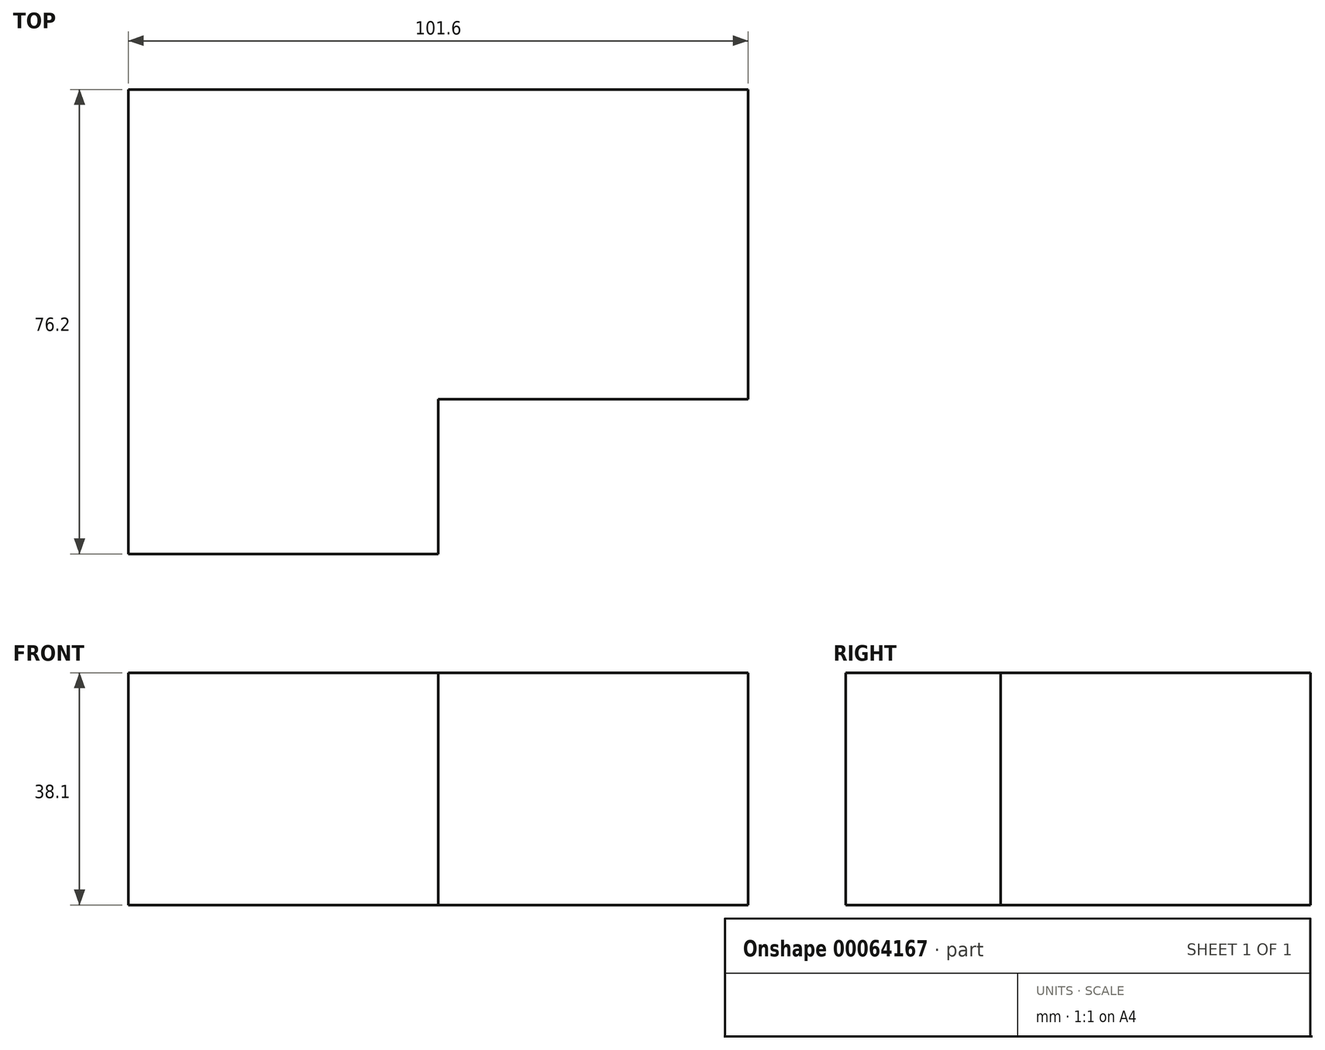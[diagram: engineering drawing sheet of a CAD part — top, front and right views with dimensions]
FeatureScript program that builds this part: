
annotation { "Feature Type Name" : "Feature", "Feature Type Description" : "" }
export const myFeature = defineFeature(function(context is Context, id is Id, definition is map)
    precondition{}
    {
        {
            var Q0;
            Q0=qCreatedBy(makeId("Front.planeOp"),FACE);
            var sketch = newSketch(context, id + "F0", { "sketchPlane" : qUnion([Q0])});
            skLineSegment(sketch, "E0.rect.bottom", {"start": v(50.8, -19.05) * mm, "end": v(-50.8, -19.05) * mm});
            skLineSegment(sketch, "E0.rect.top", {"start": v(50.8, 19.05) * mm, "end": v(-50.8, 19.05) * mm});
            skLineSegment(sketch, "E0.rect.left", {"start": v(50.8, -19.05) * mm, "end": v(50.8, 19.05) * mm});
            skLineSegment(sketch, "E0.rect.right", {"start": v(-50.8, -19.05) * mm, "end": v(-50.8, 19.05) * mm});
            skPoint(sketch, "E0.rect.middle", {"position": v(0, 0) * mm});
            skSolve(sketch);
        }
        {
            var Q0;
            Q0=makeQuery(id+"F0.imprint","IMPRINT",FACE,{"disambiguationData":[TD([[makeQuery(id+"F0.imprint","IMPRINT",EDGE,{"derivedFrom":sQuery(id+"F0.wireOp",EDGE,"E0.rect.bottom")}),-1.0]])]});
            extrude(context, id + "F1", {"entities" : qUnion([Q0]), "depth" : 25.4 * mm});
        }
        {
            var Q0;
            Q0=makeQuery(id+"F1.opExtrude","CAP_FACE",FACE,{"disambiguationData":[OSD([sQuery(id+"F0.wireOp",EDGE,"E0.rect.bottom"),sQuery(id+"F0.wireOp",EDGE,"E0.rect.top"),sQuery(id+"F0.wireOp",EDGE,"E0.rect.left"),sQuery(id+"F0.wireOp",EDGE,"E0.rect.right")])],"isStart":false});
            var sketch = newSketch(context, id + "F2", { "sketchPlane" : qUnion([Q0])});
            skLineSegment(sketch, "E1", {"start": v(0, 19.05) * mm, "end": v(0, -19.05) * mm});
            skLineSegment(sketch, "E2", {"start": v(0, -19.05) * mm, "end": v(50.8, -19.05) * mm});
            skLineSegment(sketch, "E3", {"start": v(50.8, -19.05) * mm, "end": v(50.8, 19.05) * mm});
            skLineSegment(sketch, "E4", {"start": v(50.8, 19.05) * mm, "end": v(0, 19.05) * mm});
            skSolve(sketch);
        }
        {
            var Q0;
            Q0=makeQuery(id+"F2.imprint","IMPRINT",FACE,{"disambiguationData":[TD([[makeQuery(id+"F2.imprint","IMPRINT",EDGE,{"derivedFrom":sQuery(id+"F2.wireOp",EDGE,"E1")}),1.0]])]});
            extrude(context, id + "F3", {"entities" : qUnion([Q0]), "operationType" : NewBodyOperationType.ADD, "depth" : 25.4 * mm});
        }
        {
            var Q0;
            Q0=makeQuery(id+"F1.opExtrude","CAP_FACE",FACE,{"disambiguationData":[OSD([sQuery(id+"F0.wireOp",EDGE,"E0.rect.bottom"),sQuery(id+"F0.wireOp",EDGE,"E0.rect.top"),sQuery(id+"F0.wireOp",EDGE,"E0.rect.left"),sQuery(id+"F0.wireOp",EDGE,"E0.rect.right")])],"isStart":false});
            extrude(context, id + "F4", {"entities" : qUnion([Q0]), "operationType" : NewBodyOperationType.ADD, "depth" : 50.8 * mm});
        }
    });
